# Revit family: KEUCO_34964010100
name_source: partatom
category: Möbel
revit_build: Autodesk Revit 2016 (Build: 20150220_1215(x64)
units: mm (PartAtom-declared; Revit-internal decimal feet)

## family parameters
Arbeitsebenenbasiert = Nein
Beim Laden mit Abzugskörper schneiden = Nein
Gemeinsam genutzt = Nein
Immer vertikal = Ja
Raumberechnungspunkt = Nein

## types (2) — shared parameters
Beschreibung = mit Kunststoff-Einsatz, Bürste mit verlängertem Griff
und Ersatzbürstenkopf
Gewicht = 0.628
Hersteller = KEUCO
Höhe 1 = 558 mm
Höhe 2 = 278 mm  [stored 0.912073 ft]
Kategorie = ACC
Material Abdeckung = Schwarzgrau
Preisgruppe = 1
Serie = Plan
URL = https://www.keuco.com
Verwendung = GWC / WC

## per-type parameters (varying)
| type | Ausschreibungstext | Material Bürste |
| 34964010100 | KEUCO PLAN CARE Toilettenbürstengarnitur 34964010100
hochglanzverchromte Toilettenbürstengarnitur 
in ästhetischem, funktionalem Design,
Wandmodell, komplett mit Kunststoff-Einsatz, 
Bürste mit verlängertem Griff und Ersatzbürstenkopf,
herausnehmbarer Kunststoffeinsatz für leichtes Reinigen
Höhe 278 mm (Höhe inklusive Bürste 563 mm), 
Durchmesser 104 mm, Ausladung 114 mm
Die Toilettenbürstengarnitur wird verdeckt angebracht
Lieferung inkl. korrosionsfreiem Befestigungsmaterial | Stahl, verchromt |
| 34964170100 | KEUCO PLAN CARE Toilettenbürstengarnitur 34964170100
Toilettenbürstengarnitur in Aluminium silber-eloxiert (E6 EV1),
in ästhetischem, funktionalem Design,
Wandmodell, komplett mit Kunststoff-Einsatz, 
Bürste mit verlängertem Griff und Ersatzbürstenkopf,
herausnehmbarer Kunststoffeinsatz für leichtes Reinigen
Höhe 278 mm (Höhe inklusive Bürste 563 mm), 
Durchmesser 104 mm, Ausladung 114 mm
Die Toilettenbürstengarnitur wird verdeckt angebracht
Lieferung inkl. korrosionsfreiem Befestigungsmaterial | Aluminium 1100-H18 |

note: column(s) folded — value = type name in every type: Artikelnummer

note: [stored X ft] marks values corroborated as IEEE doubles in the binary element streams (Revit-internal decimal feet)

## geometry (parser evidence)
native form markers: Blend x2, Sweep x3
no freeform markers — native parametric forms only
